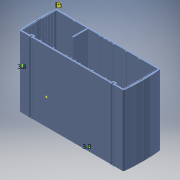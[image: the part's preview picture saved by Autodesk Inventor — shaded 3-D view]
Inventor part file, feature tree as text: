
AUTODESK INVENTOR PART (.ipt)
format: ipt  version: 2018 (Build 220112000, 112)  size: 1,251,840 bytes
history: native  units: mm
features: sketch x12, extrude x5, other x4, reference x2, imported_body x1, projected_geometry x1
ambient origin geometry x8: Origin, YZ Plane, XZ Plane, XY Plane, X Axis, Y Axis, Z Axis, Center Point
bodies: Body1 (feature_tree)
feature tree (25):
  other  "041800222_Profil_X_Dream_t220.1"
  imported_body  "Basis1"
  extrude  "Extrusion1"  Depth=4.2mm
  extrude  "Extrusion2"  Depth=93.5mm
  extrude  "Extrusion3"  Depth=8.0mm
  sketch  "Sketch5"  dims[d8=8.0mm d9=4.0mm d10=0.0mm]
  sketch  "Sketch6"  dims[d11=15.08mm d13=3.0mm]
  sketch  "Sketch7"  dims[d14=8.0mm]
  sketch  "Sketch8"  dims[d15=93.297949mm]
  sketch  "Sketch9"  dims[d16=3.0mm]
  extrude  "Extrusion6"  Depth=4.0mm TaperAngle=0.0deg
  sketch  "Sketch11"  dims[d18=6.0mm d19=0.0mm]
  sketch  "Sketch12"  dims[d20=3.8mm]
  extrude  "Extrusion7"  Depth=3.0mm
  sketch  "Sketch2"  dims[d0=32.0mm d1=0.0mm d2=4.2mm]
  sketch  "Sketch3"  dims[d3=15.08mm d4=93.5mm]
  sketch  "Sketch4"  dims[d5=4.2mm d6=93.5mm d7=8.0mm]
  sketch  "Sketch10"  dims[d17=8.0mm]
  projected_geometry  "Projected Loop1"
  reference  "Reference1"
  sketch  "Sketch13"  dims[d23=3.8mm d26=10.0mm d27=0.0mm d28=4.0mm d29=0.0mm]
  reference  "Reference2"
  other  "<userpath>\Documents\optoelectronics\CAD\Bigdriver_box\Big_housing.iam"
  other  "Big_housing.iam"
  other  "source:1"
